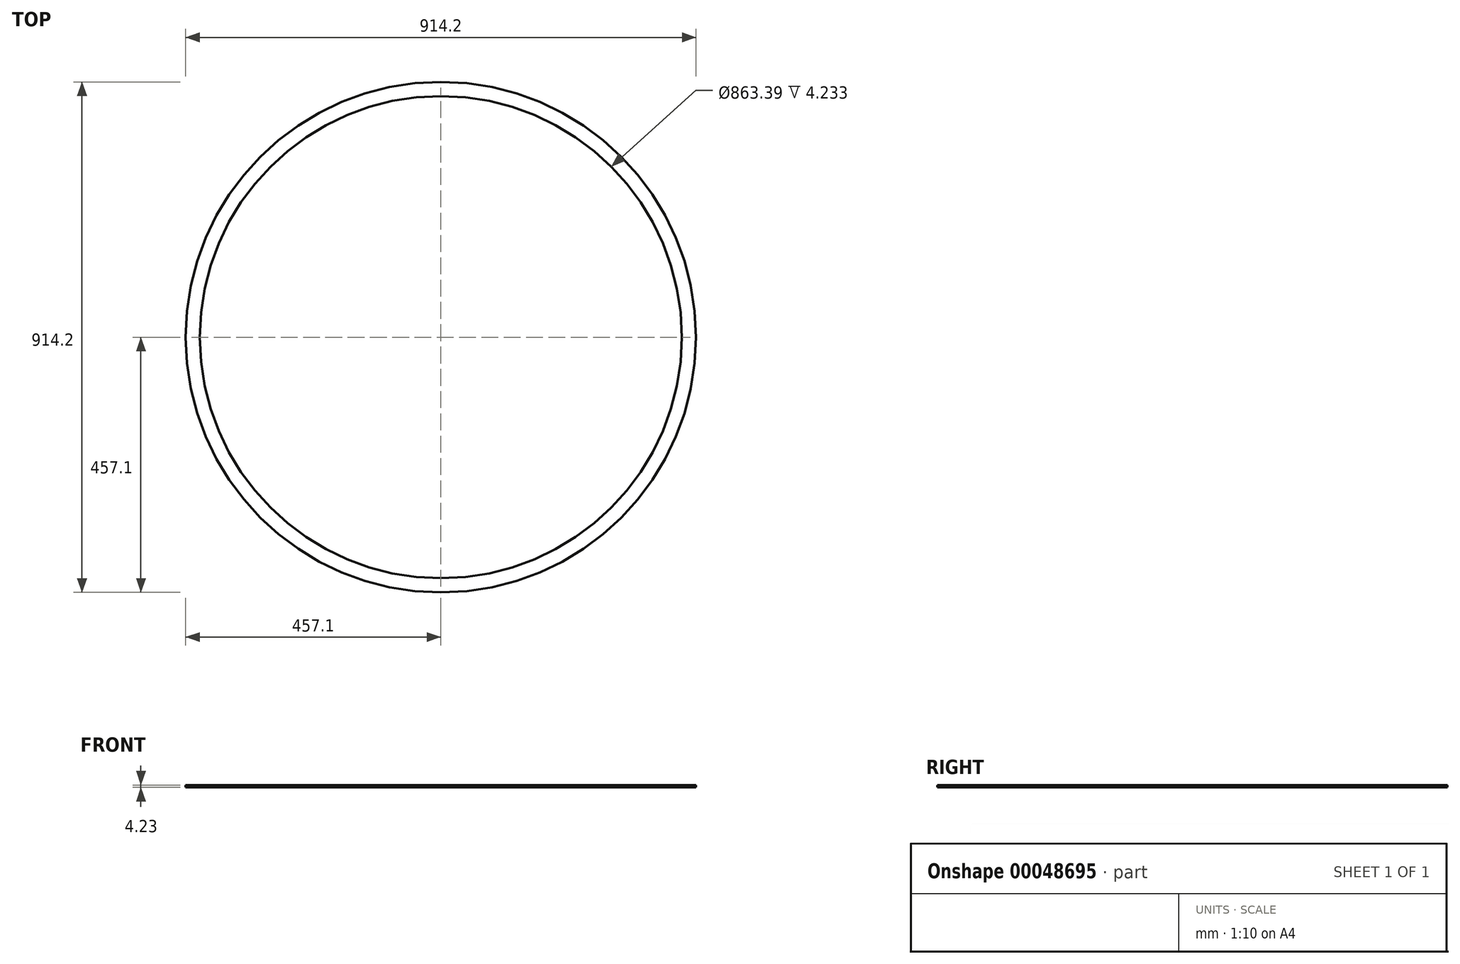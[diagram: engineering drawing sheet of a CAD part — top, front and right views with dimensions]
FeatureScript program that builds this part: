
annotation { "Feature Type Name" : "Feature", "Feature Type Description" : "" }
export const myFeature = defineFeature(function(context is Context, id is Id, definition is map)
    precondition{}
    {
        {
            var Q0;
            Q0=qCreatedBy(makeId("Top.planeOp"),FACE);
            var sketch = newSketch(context, id + "F0", { "sketchPlane" : qUnion([Q0])});
            skCircle(sketch, "E0", {"center": v(0, 0) * mm, "radius": 457.1 * mm});
            skCircle(sketch, "E1", {"center": v(0, 0) * mm, "radius": 431.7 * mm});
            skSolve(sketch);
        }
        {
            var Q0;
            Q0 = qSketchRegion(id + "F0", true);
            extrude(context, id + "F1", {"entities" : qUnion([Q0]), "depth" : 4.23 * mm});
        }
    });
